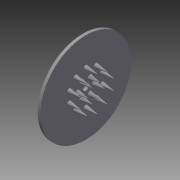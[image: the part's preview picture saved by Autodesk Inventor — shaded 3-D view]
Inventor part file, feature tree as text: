
AUTODESK INVENTOR PART (.ipt)
format: ipt  version: 2015 (Build 190159000, 159)  size: 153,088 bytes
history: native  units: in
note: dims shown in document units (in); Inventor stores cm internally (conversion verified against a paired STEP export)
features: extrude x5, sketch x5, pattern_circular x2
ambient origin geometry x8: Origin, YZ Plane, XZ Plane, XY Plane, X Axis, Y Axis, Z Axis, Center Point
bodies: Solid1 (feature_tree)
feature tree (12):
  extrude  "Extrusion1"  Depth=0.125in TaperAngle=0.0deg
  extrude  "Extrusion2"  Depth=0.5in
  pattern_circular  "Circular Pattern1"  Count=10 Angle=360.0deg
  extrude  "Extrusion3"  Depth=0.5in TaperAngle=360.0deg
  pattern_circular  "Circular Pattern2"  [2 undecoded]
  extrude  "Extrusion4"  Depth=0.125in TaperAngle=0.0deg
  extrude  "Extrusion5"  [1 undecoded]
  sketch  "Sketch1"  dims[d0=4.0in d1=0.125in d2=0.0in]
  sketch  "Sketch2"  dims[d3=0.2in d4=0.5in d5=-0.0687in d6=3.937in d7=360.0deg]
  sketch  "Sketch3"  dims[d9=0.5in d10=-0.0687in d11=2.3622in d12=360.0deg]
  sketch  "Sketch4"  dims[d14=0.43in]
  sketch  "Sketch5"  dims[d15=0.125in d16=0.0in d17=0.25in d18=0.125in d19=0.0in]
note: 3 required parameter values undecoded (feature->parameter linkage not recoverable at this tier; creation-order binding heuristic only, values carry confidence <= 0.55)
